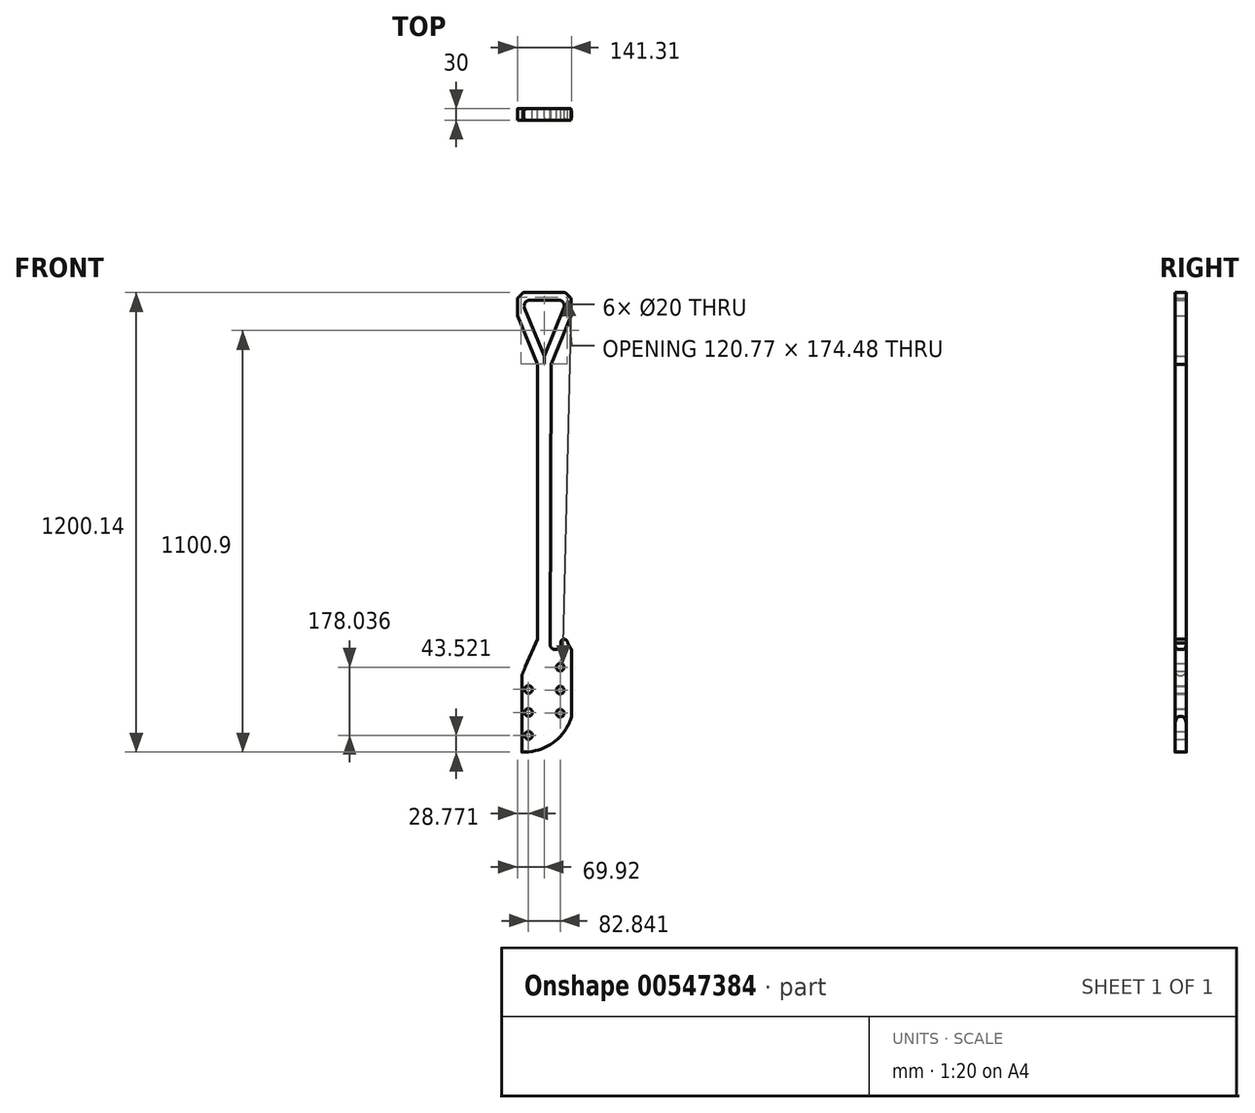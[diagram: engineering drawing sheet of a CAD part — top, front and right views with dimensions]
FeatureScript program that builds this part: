
annotation { "Feature Type Name" : "Feature", "Feature Type Description" : "" }
export const myFeature = defineFeature(function(context is Context, id is Id, definition is map)
    precondition{}
    {
        {
            var Q0;
            Q0=qCreatedBy(makeId("Front.planeOp"),FACE);
            var sketch = newSketch(context, id + "F0", { "sketchPlane" : qUnion([Q0])});
            skLineSegment(sketch, "E0.bottom", {"start": v(15.07, 0) * mm, "end": v(125.02, 0) * mm});
            skLineSegment(sketch, "E0.right", {"start": v(140.02, -14.98) * mm, "end": v(140.07, -59.59) * mm});
            skLineSegment(sketch, "E1", {"start": v(32.5, -20) * mm, "end": v(107.5, -20) * mm});
            skPoint(sketch, "E2", {"position": v(70, -20) * mm});
            skPoint(sketch, "E3", {"position": v(70, 0) * mm});
            skPoint(sketch, "E4.visualSharp", {"position": v(0, 0) * mm});
            skArc(sketch, "E4.filletArc", {"start": v(15.07, 0) * mm, "mid": v(4.4, -4.46) * mm, "end": v(0.08, -15.18) * mm});
            skPoint(sketch, "E5.visualSharp", {"position": v(140, 0) * mm});
            skArc(sketch, "E5.filletArc", {"start": v(140.02, -14.98) * mm, "mid": v(135.62, -4.39) * mm, "end": v(125.02, 0) * mm});
            skPoint(sketch, "E6", {"position": v(0.08, -60.18) * mm});
            skPoint(sketch, "E7", {"position": v(140.08, -60.18) * mm});
            skPoint(sketch, "E8", {"position": v(70, -230) * mm});
            skLineSegment(sketch, "E9", {"start": v(0.08, -60.18) * mm, "end": v(52.5, -187.5) * mm});
            skLineSegment(sketch, "E10", {"start": v(139.85, -60.73) * mm, "end": v(87.48, -187.64) * mm});
            skLineSegment(sketch, "E11", {"start": v(18.63, -40.71) * mm, "end": v(70, -165.47) * mm});
            skLineSegment(sketch, "E12", {"start": v(121.37, -40.71) * mm, "end": v(70, -165.47) * mm});
            skPoint(sketch, "E13.visualSharp", {"position": v(10.1, -20) * mm});
            skArc(sketch, "E13.filletArc", {"start": v(32.5, -20) * mm, "mid": v(20.04, -26.65) * mm, "end": v(18.63, -40.71) * mm});
            skPoint(sketch, "E14.visualSharp", {"position": v(129.9, -20) * mm});
            skArc(sketch, "E14.filletArc", {"start": v(121.37, -40.71) * mm, "mid": v(119.96, -26.65) * mm, "end": v(107.5, -20) * mm});
            skLineSegment(sketch, "E15", {"start": v(11.23, -1000.03) * mm, "end": v(11.23, -1200) * mm});
            skPoint(sketch, "E16", {"position": v(11.23, -1000) * mm});
            skPoint(sketch, "E17", {"position": v(70, -955.6) * mm});
            skLineSegment(sketch, "E18", {"start": v(11.23, -1000) * mm, "end": v(52.5, -905) * mm});
            skArc(sketch, "E19", {"start": v(85.74, -914.48) * mm, "mid": v(98.6, -932.57) * mm, "end": v(112.77, -915.46) * mm});
            skArc(sketch, "E20", {"start": v(130.69, -915.46) * mm, "mid": v(121.73, -905.62) * mm, "end": v(112.77, -915.46) * mm});
            skLineSegment(sketch, "E21", {"start": v(130.69, -915.46) * mm, "end": v(141.17, -932.23) * mm});
            skLineSegment(sketch, "E22", {"start": v(52.5, -905) * mm, "end": v(52.5, -187.5) * mm});
            skLineSegment(sketch, "E23", {"start": v(87.48, -187.64) * mm, "end": v(85.74, -914.48) * mm});
            skCircle(sketch, "E24", {"center": v(28.85, -1036.62) * mm, "radius": 10 * mm});
            skCircle(sketch, "E25", {"center": v(28.85, -1096.62) * mm, "radius": 10 * mm});
            skCircle(sketch, "E26", {"center": v(28.85, -1156.62) * mm, "radius": 10 * mm});
            skCircle(sketch, "E27", {"center": v(111.7, -978.58) * mm, "radius": 10 * mm});
            skCircle(sketch, "E28", {"center": v(111.7, -1038.58) * mm, "radius": 10 * mm});
            skCircle(sketch, "E29", {"center": v(111.7, -1098.58) * mm, "radius": 10 * mm});
            skPoint(sketch, "E30.orphan", {"position": v(52.5, -1200) * mm});
            skLineSegment(sketch, "E31", {"start": v(0.08, -15.18) * mm, "end": v(0.08, -59.59) * mm});
            skLineSegment(sketch, "E32", {"start": v(52.5, -187.5) * mm, "end": v(0.3, -60.73) * mm});
            skArc(sketch, "E33.filletArc", {"start": v(139.85, -60.73) * mm, "mid": v(140.02, -60.17) * mm, "end": v(140.07, -59.59) * mm});
            skLineSegment(sketch, "E34", {"start": v(141.17, -932.23) * mm, "end": v(141.39, -1107.33) * mm});
            skArc(sketch, "E35", {"start": v(11.23, -1200) * mm, "mid": v(92.31, -1176.15) * mm, "end": v(141.39, -1107.33) * mm});
            skLineSegment(sketch, "E36", {"start": v(0.08, -59.59) * mm, "end": v(0.08, -60.18) * mm});
            skLineSegment(sketch, "E37", {"start": v(85.74, -914.48) * mm, "end": v(87.48, -187.64) * mm});
            skLineSegment(sketch, "E38", {"start": v(87.48, -187.64) * mm, "end": v(140.08, -60.18) * mm});
            skLineSegment(sketch, "E39", {"start": v(140.08, -60.18) * mm, "end": v(140.02, -14.98) * mm});
            skLineSegment(sketch, "E40", {"start": v(125.02, 0) * mm, "end": v(140.02, -14.98) * mm});
            skLineSegment(sketch, "E41", {"start": v(125.02, 0) * mm, "end": v(15.07, 0) * mm});
            skLineSegment(sketch, "E42", {"start": v(15.07, 0) * mm, "end": v(0.08, -15.18) * mm});
            skLineSegment(sketch, "E43", {"start": v(0.08, -15.18) * mm, "end": v(0.08, -60.18) * mm});
            skLineSegment(sketch, "E44", {"start": v(52.5, -187.5) * mm, "end": v(52.5, -905) * mm});
            skLineSegment(sketch, "E45", {"start": v(52.5, -905) * mm, "end": v(11.23, -1000) * mm});
            skLineSegment(sketch, "E46", {"start": v(11.23, -1000) * mm, "end": v(11.23, -1200) * mm});
            skSolve(sketch);
        }
        {
            var Q0;
            Q0=makeQuery(id+"F0.imprint","IMPRINT",FACE,{"disambiguationData":[TD([[makeQuery(id+"F0.imprint","IMPRINT",EDGE,{"derivedFrom":sQuery(id+"F0.wireOp",EDGE,"E1")}),1.0]])]});
            extrude(context, id + "F1", {"entities" : qUnion([Q0]), "depth" : 30 * mm, "offsetDistance" : 25 * mm});
        }
        {
            var Q0;
            Q0=makeQuery(id+"F1.opExtrude","CAP_EDGE",EDGE,{"disambiguationData":[OSD([sQuery(id+"F0.wireOp",EDGE,"E44")])],"isStart":true});
            var Q1;
            Q1=makeQuery(id+"F1.opExtrude","CAP_EDGE",EDGE,{"disambiguationData":[OSD([sQuery(id+"F0.wireOp",EDGE,"E44")])],"isStart":false});
            var Q2;
            Q2=makeQuery(id+"F1.opExtrude","CAP_EDGE",EDGE,{"disambiguationData":[OSD([sQuery(id+"F0.wireOp",EDGE,"E45")])],"isStart":false});
            var Q3;
            Q3=makeQuery(id+"F1.opExtrude","CAP_EDGE",EDGE,{"disambiguationData":[OSD([sQuery(id+"F0.wireOp",EDGE,"E46")])],"isStart":false});
            var Q4;
            Q4=makeQuery(id+"F1.opExtrude","CAP_EDGE",EDGE,{"disambiguationData":[OSD([sQuery(id+"F0.wireOp",EDGE,"E46")])],"isStart":true});
            var Q5;
            Q5=makeQuery(id+"F1.opExtrude","CAP_EDGE",EDGE,{"disambiguationData":[OSD([sQuery(id+"F0.wireOp",EDGE,"E45")])],"isStart":true});
            var Q6;
            Q6=makeQuery(id+"F1.opExtrude","CAP_EDGE",EDGE,{"disambiguationData":[OSD([sQuery(id+"F0.wireOp",EDGE,"E34")])],"isStart":true});
            var Q7;
            Q7=makeQuery(id+"F1.opExtrude","CAP_EDGE",EDGE,{"disambiguationData":[OSD([sQuery(id+"F0.wireOp",EDGE,"E34")])],"isStart":false});
            fillet(context, id + "F2", {"entities" : qUnion([Q0, Q1, Q2, Q3, Q4, Q5, Q6, Q7]), "radius" : 10 * mm, "tangentPropagation" : true, "allowEdgeOverflow" : false});
        }
        {
            var Q0;
            Q0=makeQuery(id+"F1.opExtrude","CAP_EDGE",EDGE,{"disambiguationData":[OSD([sQuery(id+"F0.wireOp",EDGE,"E19")])],"isStart":false});
            var Q1;
            Q1=makeQuery(id+"F1.opExtrude","CAP_EDGE",EDGE,{"disambiguationData":[OSD([sQuery(id+"F0.wireOp",EDGE,"E19")])],"isStart":true});
            fillet(context, id + "F3", {"entities" : qUnion([Q0, Q1]), "radius" : 2 * mm, "tangentPropagation" : true, "allowEdgeOverflow" : false});
        }
        {
            var Q0;
            Q0=makeQuery(id+"F1.opExtrude","CAP_EDGE",EDGE,{"disambiguationData":[OSD([sQuery(id+"F0.wireOp",EDGE,"E41")])],"isStart":false});
            var Q1;
            Q1=makeQuery(id+"F1.opExtrude","CAP_EDGE",EDGE,{"disambiguationData":[OSD([sQuery(id+"F0.wireOp",EDGE,"E42")])],"isStart":false});
            var Q2;
            Q2=makeQuery(id+"F1.opExtrude","CAP_EDGE",EDGE,{"disambiguationData":[OSD([sQuery(id+"F0.wireOp",EDGE,"E43")])],"isStart":false});
            var Q3;
            Q3=makeQuery(id+"F1.opExtrude","CAP_EDGE",EDGE,{"disambiguationData":[OSD([sQuery(id+"F0.wireOp",EDGE,"E12")])],"isStart":false});
            var Q4;
            Q4=makeQuery(id+"F1.opExtrude","CAP_EDGE",EDGE,{"disambiguationData":[OSD([sQuery(id+"F0.wireOp",EDGE,"E9")])],"isStart":false});
            var Q5;
            Q5=makeQuery(id+"F1.opExtrude","CAP_EDGE",EDGE,{"disambiguationData":[OSD([sQuery(id+"F0.wireOp",EDGE,"E38")])],"isStart":true});
            var Q6;
            Q6=makeQuery(id+"F1.opExtrude","CAP_EDGE",EDGE,{"disambiguationData":[OSD([sQuery(id+"F0.wireOp",EDGE,"E38")])],"isStart":false});
            var Q7;
            Q7=makeQuery(id+"F1.opExtrude","CAP_EDGE",EDGE,{"disambiguationData":[OSD([sQuery(id+"F0.wireOp",EDGE,"E41")])],"isStart":true});
            var Q8;
            Q8=makeQuery(id+"F1.opExtrude","SWEPT_EDGE",EDGE,{"disambiguationData":[OSD([sQuery(id+"F0.wireOp",EDGE,"E5.filletArc"),sQuery(id+"F0.wireOp",EDGE,"E40"),sQuery(id+"F0.wireOp",EDGE,"E41")])]});
            var Q9;
            Q9=makeQuery(id+"F1.opExtrude","SWEPT_EDGE",EDGE,{"disambiguationData":[OSD([sQuery(id+"F0.wireOp",EDGE,"E5.filletArc"),sQuery(id+"F0.wireOp",EDGE,"E39"),sQuery(id+"F0.wireOp",EDGE,"E40")])]});
            var Q10;
            Q10=makeQuery(id+"F1.opExtrude","CAP_EDGE",EDGE,{"disambiguationData":[OSD([sQuery(id+"F0.wireOp",EDGE,"E11")])],"isStart":true});
            var Q11;
            Q11=makeQuery(id+"F1.opExtrude","CAP_EDGE",EDGE,{"disambiguationData":[OSD([sQuery(id+"F0.wireOp",EDGE,"E9")])],"isStart":true});
            var Q12;
            Q12=makeQuery(id+"F1.opExtrude","CAP_EDGE",EDGE,{"disambiguationData":[OSD([sQuery(id+"F0.wireOp",EDGE,"E43")])],"isStart":true});
            var Q13;
            Q13=makeQuery(id+"F1.opExtrude","CAP_EDGE",EDGE,{"disambiguationData":[OSD([sQuery(id+"F0.wireOp",EDGE,"E42")])],"isStart":true});
            fillet(context, id + "F4", {"entities" : qUnion([Q0, Q1, Q2, Q3, Q4, Q5, Q6, Q7, Q8, Q9, Q10, Q11, Q12, Q13]), "radius" : 8 * mm, "tangentPropagation" : true, "allowEdgeOverflow" : false});
        }
    });
